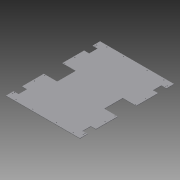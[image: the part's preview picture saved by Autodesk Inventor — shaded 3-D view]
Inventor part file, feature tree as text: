
AUTODESK INVENTOR PART (.ipt)
format: ipt  version: 2015 SP1 (Build 190203100, 203)  size: 248,832 bytes
history: native  units: in
note: dims shown in document units (in); Inventor stores cm internally (conversion verified against a paired STEP export)
features: sketch x4, hole x3, projected_geometry x3, extrude x1
ambient origin geometry x8: Origin, YZ Plane, XZ Plane, XY Plane, X Axis, Y Axis, Z Axis, Center Point
bodies: Solid1 (feature_tree)
feature tree (11):
  extrude  "Extrusion1"  Depth=28.0in
  hole  "Hole1"  [1 undecoded]
  hole  "Hole2"  [1 undecoded]
  hole  "Hole3"  [1 undecoded]
  sketch  "Sketch1"  dims[d0=22.0in d1=28.0in]
  sketch  "Sketch2"  dims[d2=4.0in d3=2.75in]
  projected_geometry  "Projected Loop1"
  sketch  "Sketch3"  dims[d4=4.0in d5=2.75in]
  projected_geometry  "Projected Loop2"
  sketch  "Sketch4"  dims[d6=4.0in d7=2.75in d8=4.0in d9=2.75in d10=2.25in d11=1.5in d12=2.5in d13=2.25in d14=1.5in d15=2.5in d16=2.25in d17=1.5in d18=2.5in d19=2.25in d20=1.5in d21=2.5in d22=0.125in d23=0.0in d24=0.5in d25=0.5in d26=2.0in d27=1.5in d28=0.5in d29=0.5in d30=1.5in d31=2.0in d32=2.0in d33=1.5in d34=1.5in d35=2.0in d36=0.5in d37=0.5in d38=0.5in d39=0.5in d40=0.25in d41=0.75in d42=0.375in d43=0.25in d44=0.5635in d45=1.0in d46=0.8108in d47=0.5in d48=0.5in d49=3.25in d50=0.25in d51=0.25in d52=3.25in d53=0.5in d54=0.5in d55=0.5in d56=0.5in d57=0.25in d58=3.25in d59=0.25in d60=0.5in d61=3.25in d62=0.5in d63=0.25in d64=0.75in d65=0.375in d66=0.25in d67=0.5635in d68=1.0in d69=0.8108in d70=2.5in d71=0.5in d72=0.5in d73=7.5in d74=2.5in d75=0.5in d76=0.5in d77=7.5in d78=0.5in d79=2.5in d80=0.5in d81=7.5in d82=2.5in d83=0.5in d84=0.5in d85=7.5in d86=0.25in d87=0.75in d88=0.375in d89=0.25in d90=0.5635in d91=1.0in d92=0.8108in]
  projected_geometry  "Projected Loop3"
note: 3 required parameter values undecoded (feature->parameter linkage not recoverable at this tier; creation-order binding heuristic only, values carry confidence <= 0.55)
